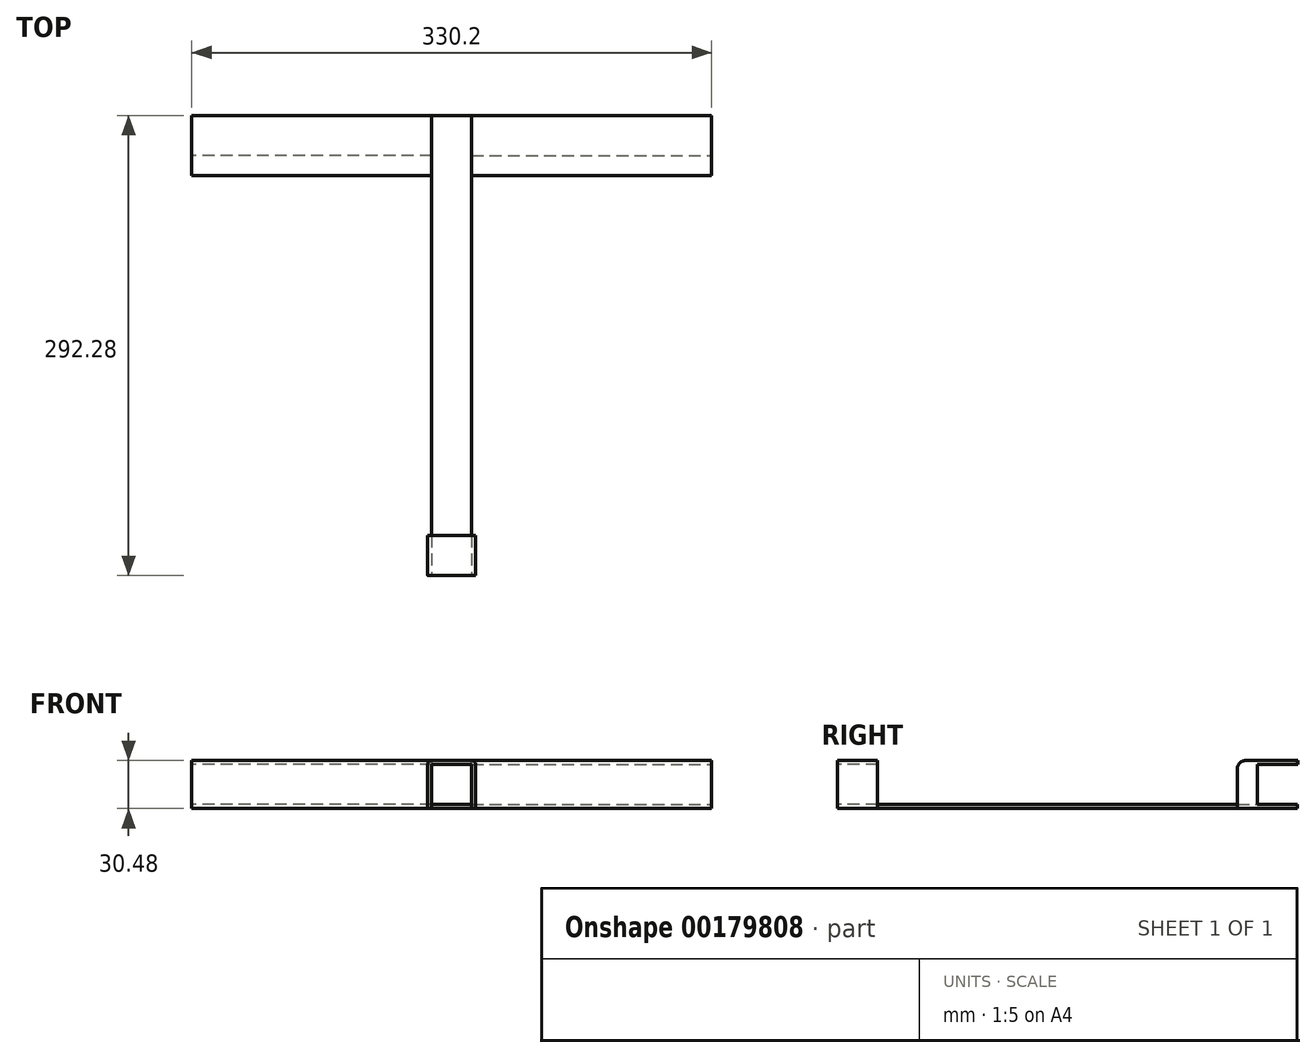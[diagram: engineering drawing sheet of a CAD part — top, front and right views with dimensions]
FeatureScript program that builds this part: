
annotation { "Feature Type Name" : "Feature", "Feature Type Description" : "" }
export const myFeature = defineFeature(function(context is Context, id is Id, definition is map)
    precondition{}
    {
        {
            var Q0;
            Q0=qCreatedBy(makeId("Top.planeOp"),FACE);
            var sketch = newSketch(context, id + "F0", { "sketchPlane" : qUnion([Q0])});
            skLineSegment(sketch, "E0.bottom", {"start": v(-87.63, 23.3) * mm, "end": v(64.77, 23.3) * mm});
            skLineSegment(sketch, "E0.top", {"start": v(-87.63, -14.8) * mm, "end": v(64.77, -14.8) * mm});
            skLineSegment(sketch, "E0.left", {"start": v(-87.63, 23.3) * mm, "end": v(-87.63, -14.8) * mm});
            skLineSegment(sketch, "E0.right", {"start": v(64.77, 23.3) * mm, "end": v(64.77, -14.8) * mm});
            skLineSegment(sketch, "E1.bottom", {"start": v(90.17, 23.3) * mm, "end": v(242.57, 23.3) * mm});
            skLineSegment(sketch, "E1.top", {"start": v(90.17, -14.8) * mm, "end": v(242.57, -14.8) * mm});
            skLineSegment(sketch, "E1.left", {"start": v(90.17, 23.3) * mm, "end": v(90.17, -14.8) * mm});
            skLineSegment(sketch, "E1.right", {"start": v(242.57, 23.3) * mm, "end": v(242.57, -14.8) * mm});
            skLineSegment(sketch, "E2", {"start": v(64.77, 23.3) * mm, "end": v(90.17, 23.3) * mm});
            skLineSegment(sketch, "E3", {"start": v(64.77, -14.8) * mm, "end": v(90.17, -14.8) * mm});
            skLineSegment(sketch, "E4", {"start": v(64.77, -14.8) * mm, "end": v(64.77, -268.8) * mm});
            skLineSegment(sketch, "E5", {"start": v(90.17, -14.8) * mm, "end": v(90.17, -268.8) * mm});
            skLineSegment(sketch, "E6", {"start": v(64.77, -268.8) * mm, "end": v(90.17, -268.8) * mm});
            skSolve(sketch);
        }
        {
            var Q0;
            Q0 = qSketchRegion(id + "F0", true);
            extrude(context, id + "F1", {"entities" : qUnion([Q0]), "depth" : 2.54 * mm});
        }
        {
            var Q0;
            Q0=makeQuery(id+"F1.opExtrude","CAP_FACE",FACE,{"disambiguationData":[OSD([sQuery(id+"F0.wireOp",EDGE,"E0.bottom"),sQuery(id+"F0.wireOp",EDGE,"E0.top"),sQuery(id+"F0.wireOp",EDGE,"E0.left"),sQuery(id+"F0.wireOp",EDGE,"E1.bottom"),sQuery(id+"F0.wireOp",EDGE,"E1.top"),sQuery(id+"F0.wireOp",EDGE,"E1.right"),sQuery(id+"F0.wireOp",EDGE,"E2"),sQuery(id+"F0.wireOp",EDGE,"E4"),sQuery(id+"F0.wireOp",EDGE,"E5"),sQuery(id+"F0.wireOp",EDGE,"E6")])],"isStart":false});
            var sketch = newSketch(context, id + "F2", { "sketchPlane" : qUnion([Q0])});
            skLineSegment(sketch, "E7", {"start": v(64.77, -14.8) * mm, "end": v(64.77, -2.1) * mm});
            skLineSegment(sketch, "E8", {"start": v(64.77, -2.1) * mm, "end": v(-87.63, -2.1) * mm});
            skLineSegment(sketch, "E9", {"start": v(-87.63, -2.1) * mm, "end": v(-87.63, -14.8) * mm});
            skLineSegment(sketch, "E10", {"start": v(-87.63, -14.8) * mm, "end": v(64.77, -14.8) * mm});
            skLineSegment(sketch, "E11", {"start": v(90.17, -14.8) * mm, "end": v(90.17, -2.1) * mm});
            skLineSegment(sketch, "E12", {"start": v(90.17, -2.1) * mm, "end": v(242.57, -2.1) * mm});
            skLineSegment(sketch, "E13", {"start": v(242.57, -2.1) * mm, "end": v(242.57, -14.8) * mm});
            skLineSegment(sketch, "E14", {"start": v(242.57, -14.8) * mm, "end": v(90.17, -14.8) * mm});
            skSolve(sketch);
        }
        {
            var Q0;
            Q0=makeQuery(id+"F2.imprint","IMPRINT",FACE,{"disambiguationData":[TD([[makeQuery(id+"F2.imprint","IMPRINT",EDGE,{"derivedFrom":sQuery(id+"F2.wireOp",EDGE,"E7")}),1.0]])]});
            var Q1;
            Q1=makeQuery(id+"F2.imprint","IMPRINT",FACE,{"disambiguationData":[TD([[makeQuery(id+"F2.imprint","IMPRINT",EDGE,{"derivedFrom":sQuery(id+"F2.wireOp",EDGE,"E11")}),-1.0]])]});
            extrude(context, id + "F3", {"entities" : qUnion([Q0, Q1]), "operationType" : NewBodyOperationType.ADD, "depth" : 25.4 * mm});
        }
        {
            var Q0;
            Q0=makeQuery(id+"F3.opExtrude","CAP_FACE",FACE,{"disambiguationData":[OSD([sQuery(id+"F2.wireOp",EDGE,"E7"),sQuery(id+"F2.wireOp",EDGE,"E8"),sQuery(id+"F2.wireOp",EDGE,"E9"),sQuery(id+"F2.wireOp",EDGE,"E10")])],"isStart":false});
            var sketch = newSketch(context, id + "F4", { "sketchPlane" : qUnion([Q0])});
            skLineSegment(sketch, "E15", {"start": v(-87.63, -14.8) * mm, "end": v(-87.63, 23.47) * mm});
            skLineSegment(sketch, "E16", {"start": v(-87.63, 23.47) * mm, "end": v(64.77, 23.47) * mm});
            skLineSegment(sketch, "E17", {"start": v(64.77, 23.47) * mm, "end": v(64.77, -14.8) * mm});
            skLineSegment(sketch, "E18", {"start": v(64.77, -14.8) * mm, "end": v(-87.63, -14.8) * mm});
            skSolve(sketch);
        }
        {
            var Q0;
            {var subQ2=sQuery(id+"F4.wireOp",EDGE,"E16");Q0=makeQuery(id+"F4.imprint","IMPRINT",FACE,{"disambiguationData":[TD([[makeQuery(id+"F4.imprint","IMPRINT",EDGE,{"derivedFrom":subQ2}),-1.0]])]});}
            var Q1;
            {var subQ0=sQuery(id+"F4.wireOp",EDGE,"E18");Q1=makeQuery(id+"F4.imprint","IMPRINT",FACE,{"disambiguationData":[TD([[makeQuery(id+"F4.imprint","IMPRINT",EDGE,{"derivedFrom":subQ0}),1.0]])]});}
            extrude(context, id + "F5", {"entities" : qUnion([Q0, Q1]), "operationType" : NewBodyOperationType.ADD, "depth" : 2.54 * mm});
        }
        {
            var Q0;
            Q0=makeQuery(id+"F3.opExtrude","CAP_FACE",FACE,{"disambiguationData":[OSD([sQuery(id+"F2.wireOp",EDGE,"E11"),sQuery(id+"F2.wireOp",EDGE,"E12"),sQuery(id+"F2.wireOp",EDGE,"E13"),sQuery(id+"F2.wireOp",EDGE,"E14")])],"isStart":false});
            var sketch = newSketch(context, id + "F6", { "sketchPlane" : qUnion([Q0])});
            skLineSegment(sketch, "E19", {"start": v(90.17, -14.8) * mm, "end": v(90.17, 23.19) * mm});
            skLineSegment(sketch, "E20", {"start": v(90.17, 23.19) * mm, "end": v(242.57, 23.19) * mm});
            skLineSegment(sketch, "E21", {"start": v(242.57, 23.19) * mm, "end": v(242.57, -14.8) * mm});
            skLineSegment(sketch, "E22", {"start": v(242.57, -14.8) * mm, "end": v(90.17, -14.8) * mm});
            skSolve(sketch);
        }
        {
            var Q0;
            {var subQ2=sQuery(id+"F6.wireOp",EDGE,"E20");Q0=makeQuery(id+"F6.imprint","IMPRINT",FACE,{"disambiguationData":[TD([[makeQuery(id+"F6.imprint","IMPRINT",EDGE,{"derivedFrom":subQ2}),-1.0]])]});}
            var Q1;
            {var subQ0=sQuery(id+"F6.wireOp",EDGE,"E22");Q1=makeQuery(id+"F6.imprint","IMPRINT",FACE,{"disambiguationData":[TD([[makeQuery(id+"F6.imprint","IMPRINT",EDGE,{"derivedFrom":subQ0}),1.0]])]});}
            extrude(context, id + "F7", {"entities" : qUnion([Q0, Q1]), "operationType" : NewBodyOperationType.ADD, "depth" : 2.54 * mm});
        }
        {
            var Q0;
            Q0=makeQuery(id+"F1.opExtrude","SWEPT_FACE",FACE,{"disambiguationData":[OSD([sQuery(id+"F0.wireOp",EDGE,"E6")])]});
            var sketch = newSketch(context, id + "F8", { "sketchPlane" : qUnion([Q0])});
            skLineSegment(sketch, "E23", {"start": v(64.77, 0) * mm, "end": v(62.23, 0) * mm});
            skLineSegment(sketch, "E24", {"start": v(62.23, 0) * mm, "end": v(62.23, 30.48) * mm});
            skLineSegment(sketch, "E25", {"start": v(62.23, 30.48) * mm, "end": v(92.71, 30.48) * mm});
            skLineSegment(sketch, "E26", {"start": v(92.71, 30.48) * mm, "end": v(92.71, 0) * mm});
            skLineSegment(sketch, "E27", {"start": v(92.71, 0) * mm, "end": v(64.77, 0) * mm});
            skLineSegment(sketch, "E28", {"start": v(64.77, 0) * mm, "end": v(64.77, 2.54) * mm});
            skLineSegment(sketch, "E29", {"start": v(64.77, 2.54) * mm, "end": v(90.17, 2.54) * mm});
            skLineSegment(sketch, "E30", {"start": v(90.17, 2.54) * mm, "end": v(90.17, 0) * mm});
            skLineSegment(sketch, "E31", {"start": v(90.17, 0) * mm, "end": v(92.71, 0) * mm});
            skLineSegment(sketch, "E32", {"start": v(64.77, 2.54) * mm, "end": v(64.77, 27.94) * mm});
            skLineSegment(sketch, "E33", {"start": v(64.77, 27.94) * mm, "end": v(90.17, 27.94) * mm});
            skLineSegment(sketch, "E34", {"start": v(90.17, 27.94) * mm, "end": v(90.17, 2.54) * mm});
            skSolve(sketch);
        }
        {
            var Q0;
            Q0=makeQuery(id+"F8.imprint","IMPRINT",FACE,{"disambiguationData":[TD([[makeQuery(id+"F8.imprint","IMPRINT",EDGE,{"derivedFrom":sQuery(id+"F8.wireOp",EDGE,"E23")}),-1.0]])]});
            extrude(context, id + "F9", {"entities" : qUnion([Q0]), "oppositeDirection" : true, "depth" : 25.4 * mm});
        }
        {
            var Q0;
            Q0=makeQuery(id+"F9.opExtrude","SWEPT_EDGE",EDGE,{"disambiguationData":[OSD([sQuery(id+"F8.wireOp",EDGE,"E25"),sQuery(id+"F8.wireOp",EDGE,"E26")])]});
            fillet(context, id + "F10", {"entities" : qUnion([Q0]), "radius" : 2.54 * mm, "tangentPropagation" : true, "allowEdgeOverflow" : false});
        }
        {
            var Q0;
            Q0=makeQuery(id+"F9.opExtrude","SWEPT_EDGE",EDGE,{"disambiguationData":[OSD([sQuery(id+"F8.wireOp",EDGE,"E24"),sQuery(id+"F8.wireOp",EDGE,"E25")])]});
            fillet(context, id + "F11", {"entities" : qUnion([Q0]), "radius" : 2.54 * mm, "tangentPropagation" : true, "allowEdgeOverflow" : false});
        }
        {
            var Q0;
            Q0=makeQuery(id+"F7.opExtrude","CAP_EDGE",EDGE,{"disambiguationData":[OSD([sQuery(id+"F6.wireOp",EDGE,"E22")])],"isStart":false});
            fillet(context, id + "F12", {"entities" : qUnion([Q0]), "radius" : 5.08 * mm, "tangentPropagation" : true, "allowEdgeOverflow" : false});
        }
        {
            var Q0;
            Q0=makeQuery(id+"F5.opExtrude","CAP_EDGE",EDGE,{"disambiguationData":[OSD([sQuery(id+"F4.wireOp",EDGE,"E18")])],"isStart":false});
            fillet(context, id + "F13", {"entities" : qUnion([Q0]), "radius" : 5.08 * mm, "tangentPropagation" : true, "allowEdgeOverflow" : false});
        }
    });
